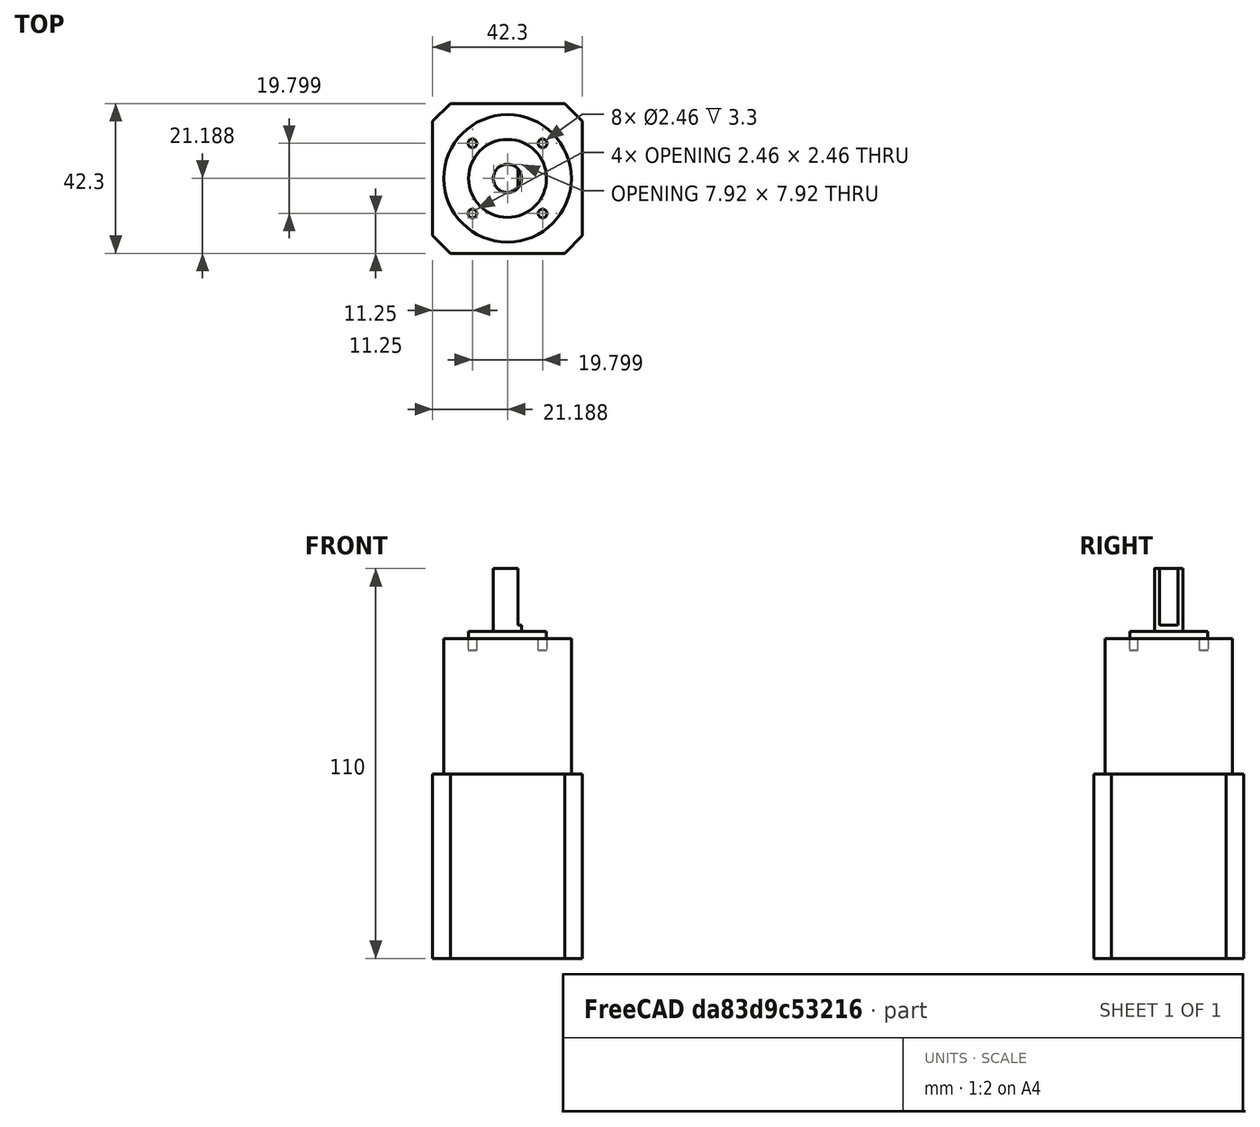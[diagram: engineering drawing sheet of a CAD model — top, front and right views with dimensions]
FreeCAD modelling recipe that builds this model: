
FCSTD DOCUMENT  (FreeCAD 0.17R13387 (Git))
Label: Motor PG100
License: All rights reserved
LicenseURL: http://en.wikipedia.org/wiki/All_rights_reserved
objects: Part::Cylinder×4, Part::Feature×3, Part::MultiFuse×2, Part::Cut×2, Part::Extrusion×1, Part::Box×1
note: 13 computed .brp shape members not serialized (recipe doc carries the construction recipe); baked Part::Feature solids carry a one-line shape summary decoded from their .brp

FEATURE [Part::Feature] Part__Feature003  label="Motor"
  Placement = pos=(0,0,11) rot=(0,0,1;1.5708rad)
  shape: bbox 42.3 x 42.3 x 87.3 mm, 26 faces (baked)
FEATURE [Part::Cylinder] Cylinder  label="Válec"
  Angle = 360
  AttacherType = Attacher::AttachEngine3D
  Height = 35
  Radius = 18
FEATURE [Part::Feature] Part__Feature003_cs
  shape: bbox 42.3 x 42.3 x 3e-07 mm, 0 faces, 0 solids (baked)
FEATURE [Part::Extrusion] Extrude
  Base = -> Part__Feature003_cs
  Dir = (0,0,1)
  DirMode = 2
  FaceMakerClass = Part::FaceMakerBullseye
  LengthFwd = -52
  LengthRev = 0
  Solid = true
  Symmetric = false
FEATURE [Part::Cylinder] Cylinder001  label="Válec001"
  Angle = 360
  AttacherType = Attacher::AttachEngine3D
  Height = 60
  Placement = pos=(0,0,-38) rot=(0,0,1;0rad)
  Radius = 30
FEATURE [Part::Cylinder] Cylinder002  label="Válec002"
  Angle = 360
  AttacherType = Attacher::AttachEngine3D
  Height = 60
  Placement = pos=(0,0,42) rot=(0,0,1;0rad)
  Radius = 8
FEATURE [Part::MultiFuse] Fusion
  Shapes = -> [Cylinder001,Cylinder002]
FEATURE [Part::Cut] Cut
  Base = -> Part__Feature003
  Tool = -> Fusion
FEATURE [Part::Cylinder] Cylinder003  label="Válec003"
  Angle = 360
  AttacherType = Attacher::AttachEngine3D
  Height = 18
  Placement = pos=(0,0,40) rot=(0,0,1;0rad)
  Radius = 4
FEATURE [Part::MultiFuse] Fusion001  label="Motor PG20"
  Shapes = -> [Cylinder,Extrude,Cut,Cylinder003]
FEATURE [Part::Box] Box  label="Krychle"
  AttacherType = Attacher::AttachEngine3D
  Height = 16
  Length = 8
  Placement = pos=(3,-4,42) rot=(0,0,1;0rad)
  Width = 8
FEATURE [Part::Cut] Cut001
  Base = -> Fusion001
  Tool = -> Box
FEATURE [Part::Feature] Cut001001  label="Motor PG100"
  shape: bbox 42.3 x 42.3 x 110 mm, 26 faces (baked)
